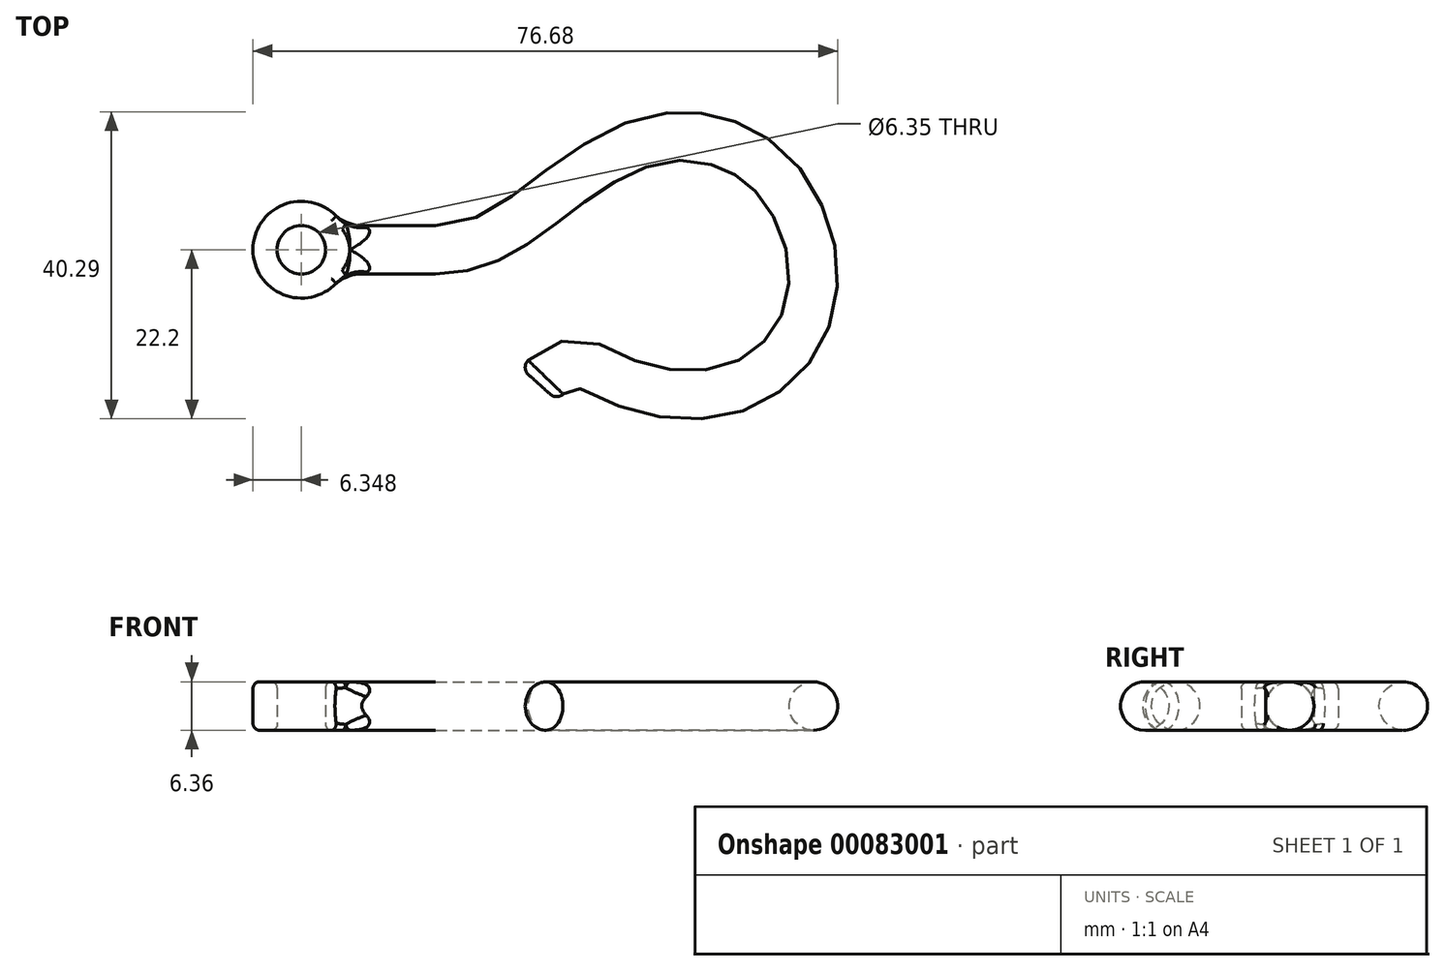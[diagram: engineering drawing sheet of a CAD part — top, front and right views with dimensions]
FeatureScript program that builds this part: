
annotation { "Feature Type Name" : "Feature", "Feature Type Description" : "" }
export const myFeature = defineFeature(function(context is Context, id is Id, definition is map)
    precondition{}
    {
        {
            var Q0;
            Q0=qCreatedBy(makeId("Top.planeOp"),FACE);
            var sketch = newSketch(context, id + "F0", { "sketchPlane" : qUnion([Q0])});
            skLineSegment(sketch, "E0", {"start": v(0, 0) * mm, "end": v(12.33, 0) * mm});
            skFitSpline(sketch, "E1", {"points": [v(12.33, 0) * mm, v(26.63, 6.29) * mm, v(41.92, 14.67) * mm, v(56.46, 9.99) * mm, v(61.64, -6.53) * mm, v(52.27, -17.88) * mm, v(36.5, -17.14) * mm, v(25.89, -17.63) * mm], "startDerivative": vector(124.43, 0) * mm, "endDerivative": vector(-105.61, -117.35) * mm});
            skSolve(sketch);
        }
        {
            var Q0;
            Q0=qCreatedBy(makeId("Right.planeOp"),FACE);
            var sketch = newSketch(context, id + "F1", { "sketchPlane" : qUnion([Q0])});
            skCircle(sketch, "E2", {"center": v(0, 0) * mm, "radius": 3.18 * mm});
            skSolve(sketch);
        }
        {
            var Q0;
            Q0 = qSketchRegion(id + "F0", true);
            var Q1;
            Q1 = qSketchRegion(id + "F1", true);
            var Q2;
            Q2=sQuery(id+"F0.wireOp",EDGE,"E0");
            var Q3;
            Q3=sQuery(id+"F0.wireOp",EDGE,"E1");
            sweep(context, id + "F2", {"profiles" : qUnion([Q0, Q1]), "path" : qUnion([Q2, Q3])});
        }
        {
            var Q0;
            Q0=qCreatedBy(makeId("Top.planeOp"),FACE);
            var sketch = newSketch(context, id + "F3", { "sketchPlane" : qUnion([Q0])});
            skCircle(sketch, "E3", {"center": v(-5.26, 0) * mm, "radius": 6.35 * mm});
            skCircle(sketch, "E4", {"center": v(-5.26, 0) * mm, "radius": 3.18 * mm});
            skSolve(sketch);
        }
        {
            var Q0;
            Q0 = qSketchRegion(id + "F3", true);
            extrude(context, id + "F4", {"entities" : qUnion([Q0]), "operationType" : NewBodyOperationType.ADD, "endBound" : BoundingType.SYMMETRIC, "depth" : 6.35 * mm});
        }
        {
            var Q0;
            Q0=makeQuery(id+"F2.opSweep","CAP_EDGE",EDGE,{"disambiguationData":[OSD([sQuery(id+"F0.wireOp",VERTEX,"E1.end"),sQuery(id+"F1.wireOp",EDGE,"E2")])],"isStart":false});
            fillet(context, id + "F5", {"entities" : qUnion([Q0]), "radius" : 1.27 * mm, "tangentPropagation" : true, "allowEdgeOverflow" : false});
        }
        {
            var Q0;
            Q0=makeQuery(id+"F4.boolean.opBoolean","INTERSECT",EDGE,{"disambiguationData":[OD(0.0)],"derivedFrom":[makeQuery(id+"F2.opSweep","SWEPT_FACE",FACE,{"disambiguationData":[OSD([sQuery(id+"F0.wireOp",EDGE,"E0"),sQuery(id+"F1.wireOp",EDGE,"E2")])]}),makeQuery(id+"F4.opExtrude","SWEPT_FACE",FACE,{"disambiguationData":[OSD([sQuery(id+"F3.wireOp",EDGE,"E3")])]})]});
            fillet(context, id + "F6", {"entities" : qUnion([Q0]), "radius" : 5.08 * mm, "tangentPropagation" : true, "allowEdgeOverflow" : false});
        }
        {
            var Q0;
            Q0=makeQuery(id+"F4.opExtrude","CAP_EDGE",EDGE,{"disambiguationData":[OSD([sQuery(id+"F3.wireOp",EDGE,"E3")])],"isStart":false});
            var Q1;
            Q1=makeQuery(id+"F4.opExtrude","CAP_EDGE",EDGE,{"disambiguationData":[OSD([sQuery(id+"F3.wireOp",EDGE,"E3")])],"isStart":true});
            fillet(context, id + "F7", {"entities" : qUnion([Q0, Q1]), "radius" : 0.89 * mm, "tangentPropagation" : true, "allowEdgeOverflow" : false});
        }
        {
            var Q0;
            Q0=makeQuery(id+"F4.opExtrude","CAP_EDGE",EDGE,{"disambiguationData":[OSD([sQuery(id+"F3.wireOp",EDGE,"E4")])],"isStart":false});
            var Q1;
            Q1=makeQuery(id+"F4.opExtrude","CAP_EDGE",EDGE,{"disambiguationData":[OSD([sQuery(id+"F3.wireOp",EDGE,"E4")])],"isStart":true});
            fillet(context, id + "F8", {"entities" : qUnion([Q0, Q1]), "radius" : 0.76 * mm, "tangentPropagation" : true, "allowEdgeOverflow" : false});
        }
    });
